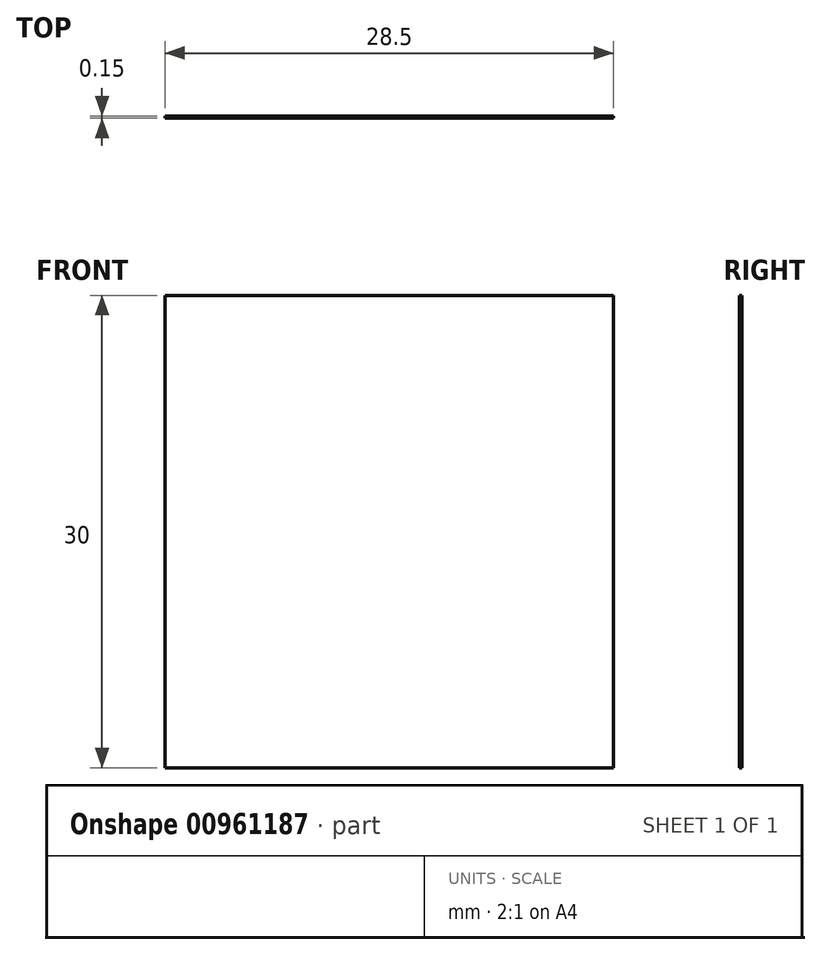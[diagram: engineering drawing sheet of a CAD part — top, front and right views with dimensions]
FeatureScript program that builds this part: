
annotation { "Feature Type Name" : "Feature", "Feature Type Description" : "" }
export const myFeature = defineFeature(function(context is Context, id is Id, definition is map)
    precondition{}
    {
        {
            var Q0;
            Q0=qCreatedBy(makeId("Front.planeOp"),FACE);
            var sketch = newSketch(context, id + "F0", { "sketchPlane" : qUnion([Q0])});
            skLineSegment(sketch, "E0.bottom", {"start": v(-12.4, 33.44) * mm, "end": v(16.1, 33.44) * mm});
            skLineSegment(sketch, "E0.top", {"start": v(-12.4, 3.44) * mm, "end": v(16.1, 3.44) * mm});
            skLineSegment(sketch, "E0.left", {"start": v(-12.4, 33.44) * mm, "end": v(-12.4, 3.44) * mm});
            skLineSegment(sketch, "E0.right", {"start": v(16.1, 33.44) * mm, "end": v(16.1, 3.44) * mm});
            skSolve(sketch);
        }
        {
            var Q0;
            Q0=makeQuery(id+"F0.imprint","IMPRINT",FACE,{"disambiguationData":[TD([[makeQuery(id+"F0.imprint","IMPRINT",EDGE,{"derivedFrom":sQuery(id+"F0.wireOp",EDGE,"E0.bottom")}),-1.0]])]});
            extrude(context, id + "F1", {"entities" : qUnion([Q0]), "depth" : .15 * mm, "offsetDistance" : 25.4 * mm});
        }
    });
